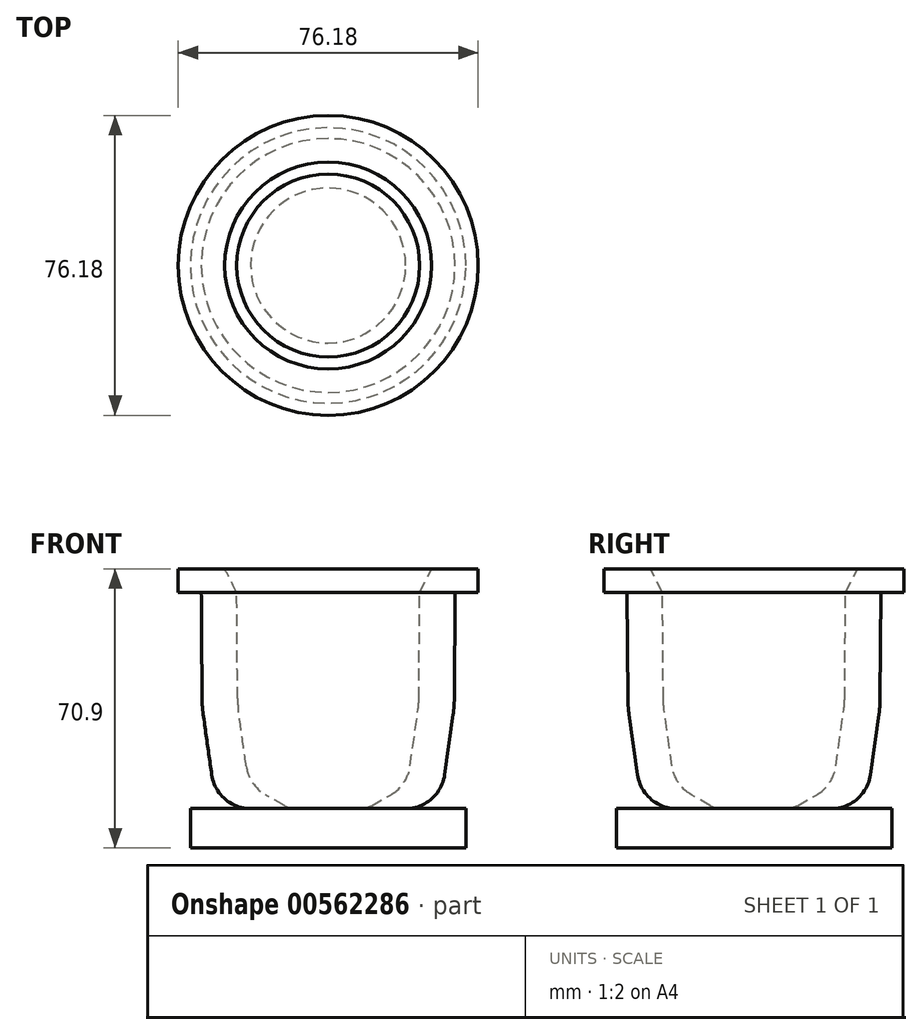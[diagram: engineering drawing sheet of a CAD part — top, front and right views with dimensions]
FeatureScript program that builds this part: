
annotation { "Feature Type Name" : "Feature", "Feature Type Description" : "" }
export const myFeature = defineFeature(function(context is Context, id is Id, definition is map)
    precondition{}
    {
        {
            var Q0;
            Q0=qCreatedBy(makeId("Top.planeOp"),FACE);
            var sketch = newSketch(context, id + "F0", { "sketchPlane" : qUnion([Q0])});
            skCircle(sketch, "E0", {"center": v(0, 0) * mm, "radius": 35 * mm});
            skSolve(sketch);
        }
        {
            var Q0;
            Q0=qSketchRegion(id+"F0",true);
            extrude(context, id + "F1", {"entities" : qUnion([Q0]), "depth" : 10 * mm});
        }
        {
            var Q0;
            Q0=qCreatedBy(makeId("Front.planeOp"),FACE);
            var sketch = newSketch(context, id + "F2", { "sketchPlane" : qUnion([Q0])});
            skLineSegment(sketch, "E1", {"start": v(-38.1, 70.9) * mm, "end": v(-38.1, 64.87) * mm});
            skLineSegment(sketch, "E2", {"start": v(-38.1, 64.87) * mm, "end": v(-32.24, 64.87) * mm});
            skLineSegment(sketch, "E3", {"start": v(-32.24, 64.87) * mm, "end": v(-32.04, 37.9) * mm});
            skLineSegment(sketch, "E4", {"start": v(-31.75, 33.96) * mm, "end": v(-29.6, 18.6) * mm});
            skPoint(sketch, "E5.visualSharp", {"position": v(-32.03, 35.92) * mm});
            skArc(sketch, "E5.filletArc", {"start": v(-32.04, 37.9) * mm, "mid": v(-31.96, 35.93) * mm, "end": v(-31.75, 33.96) * mm});
            skPoint(sketch, "E6.start.orphan", {"position": v(0, 70.9) * mm});
            skLineSegment(sketch, "E7", {"start": v(-38.1, 70.9) * mm, "end": v(-26.28, 70.9) * mm});
            skLineSegment(sketch, "E8", {"start": v(0, -18.5) * mm, "end": v(0, 74.52) * mm, "construction": true});
            skArc(sketch, "E9.filletArc", {"start": v(-29.6, 18.6) * mm, "mid": v(-26.25, 12.45) * mm, "end": v(-19.7, 10) * mm});
            skPoint(sketch, "E10.visualSharp", {"position": v(-24.52, 11.24) * mm});
            skLineSegment(sketch, "E11", {"start": v(-19.7, 10) * mm, "end": v(0, 10) * mm});
            skLineSegment(sketch, "E12.1", {"start": v(-22.84, 35.2) * mm, "end": v(-20.81, 20.78) * mm});
            skArc(sketch, "E12.2", {"start": v(-23.04, 37.98) * mm, "mid": v(-22.99, 36.59) * mm, "end": v(-22.84, 35.2) * mm});
            skLineSegment(sketch, "E12.3", {"start": v(-23.24, 64.94) * mm, "end": v(-23.04, 37.98) * mm});
            skLineSegment(sketch, "E13", {"start": v(-26.28, 70.9) * mm, "end": v(-23.24, 64.94) * mm});
            skLineSegment(sketch, "E14", {"start": v(-15.92, 13.52) * mm, "end": v(-11, 10.67) * mm});
            skLineSegment(sketch, "E15", {"start": v(-8.5, 10) * mm, "end": v(0, 10) * mm});
            skPoint(sketch, "E16.visualSharp", {"position": v(-9.85, 10) * mm});
            skArc(sketch, "E16.filletArc", {"start": v(-11, 10.67) * mm, "mid": v(-9.8, 10.17) * mm, "end": v(-8.5, 10) * mm});
            skPoint(sketch, "E17.visualSharp", {"position": v(-20.13, 15.96) * mm});
            skArc(sketch, "E17.filletArc", {"start": v(-20.81, 20.78) * mm, "mid": v(-19.2, 16.6) * mm, "end": v(-15.92, 13.52) * mm});
            skSolve(sketch);
        }
        {
            var Q0;
            Q0=makeQuery(id+"F2.imprint","IMPRINT",FACE,{"disambiguationData":[TD([[makeQuery(id+"F2.imprint","IMPRINT",EDGE,{"derivedFrom":sQuery(id+"F2.wireOp",EDGE,"E1")}),1.0]])]});
            var Q1;
            Q1=sQuery(id+"F2.wireOp",EDGE,"E8");
            revolve(context, id + "F3", {"operationType" : NewBodyOperationType.ADD, "entities" : qUnion([Q0]), "axis" : qUnion([Q1]), "revolveType" : RevolveType.FULL});
        }
    });
